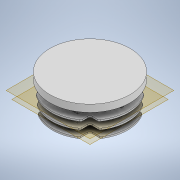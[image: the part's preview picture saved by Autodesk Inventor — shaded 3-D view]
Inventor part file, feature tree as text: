
AUTODESK INVENTOR PART (.ipt)
format: ipt  version: 2020.2 (Build 242310000, 310)  size: 353,280 bytes
history: native  units: mm
features: extrude x5, sketch x5, other x2, fillet x2
ambient origin geometry x8: Origin, YZ Plane, XZ Plane, XY Plane, X Axis, Y Axis, Z Axis, Center Point
bodies: Solide1 (feature_tree)
feature tree (14):
  extrude  "Extrusion1"  Depth=15.2mm
  extrude  "Extrusion2"  Depth=27.1mm
  extrude  "Extrusion4"  Depth=1.3mm
  other  "Plan de construction2"
  extrude  "Extrusion5"  Depth=31.0mm
  other  "Plan de construction3"
  extrude  "Extrusion6"  Depth=15.35mm TaperAngle=0.0deg
  fillet  "Congé1"  Radius=1.3mm
  fillet  "Congé2"  Radius=5.6mm
  sketch  "Esquisse1"
  sketch  "Esquisse2"
  sketch  "Esquisse5"
  sketch  "Esquisse6"
  sketch  "Esquisse7"
